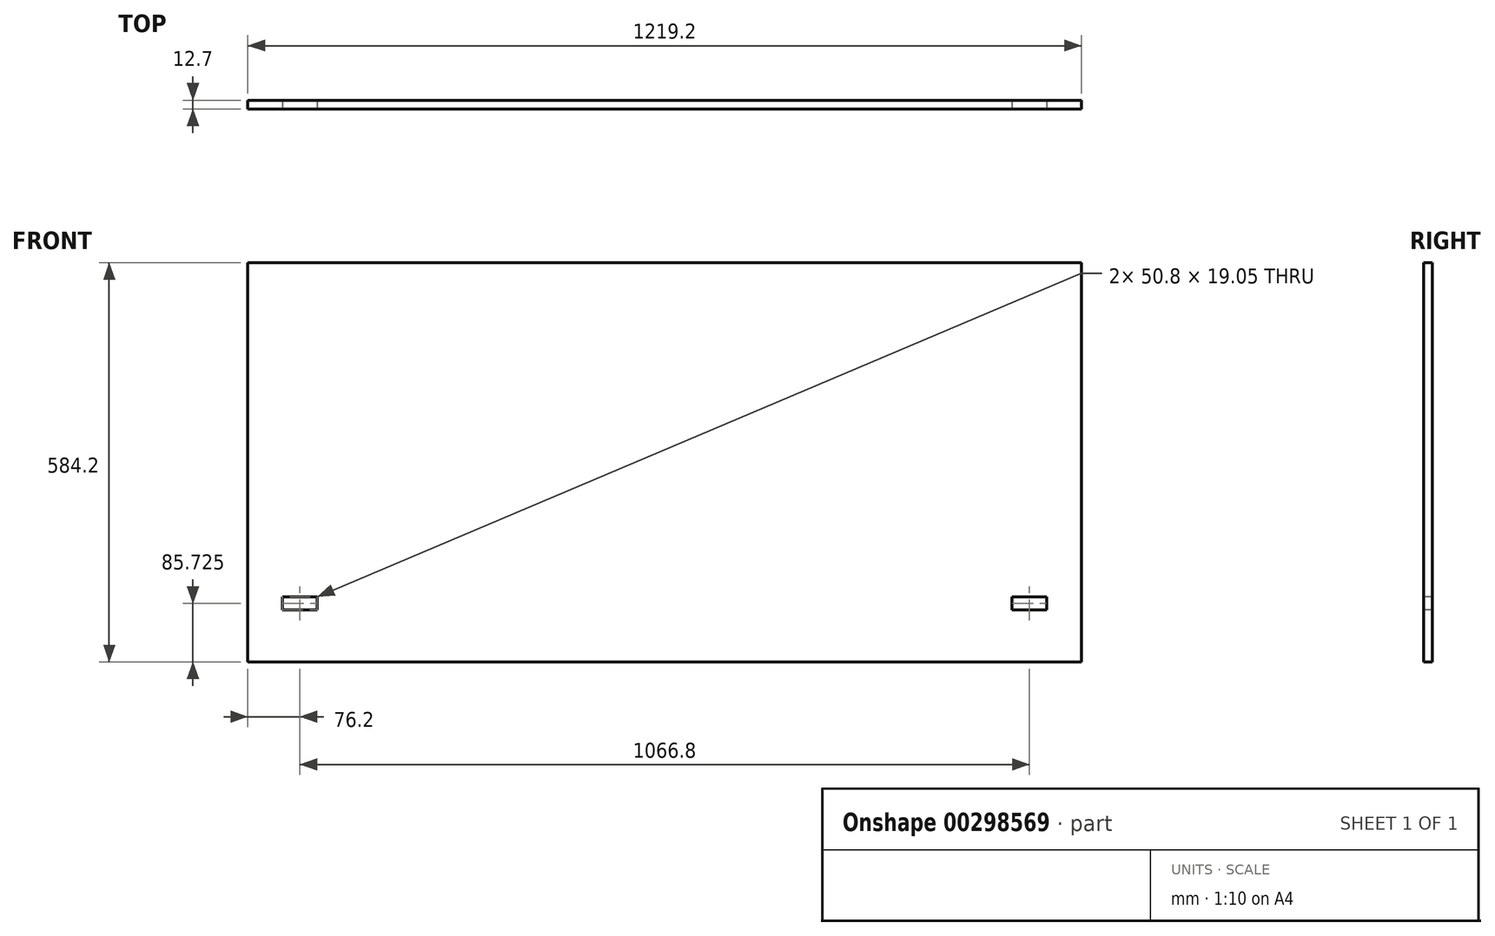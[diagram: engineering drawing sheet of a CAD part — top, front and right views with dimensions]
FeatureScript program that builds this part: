
annotation { "Feature Type Name" : "Feature", "Feature Type Description" : "" }
export const myFeature = defineFeature(function(context is Context, id is Id, definition is map)
    precondition{}
    {
        {
            assignVariable(context, id + "F0", {"name" : "thickness", "anyValue" : 12.7 * mm});
        }
        {
            var Q0;
            Q0=qCreatedBy(makeId("Front.planeOp"),FACE);
            var sketch = newSketch(context, id + "F1", { "sketchPlane" : qUnion([Q0])});
            skLineSegment(sketch, "E0", {"start": v(0, 0) * mm, "end": v(-609.6, 0) * mm});
            skLineSegment(sketch, "E1", {"start": v(-609.6, 584.2) * mm, "end": v(0, 584.2) * mm});
            skLineSegment(sketch, "E2", {"start": v(0, 584.2) * mm, "end": v(0, 0) * mm});
            skLineSegment(sketch, "E3", {"start": v(-609.6, 584.2) * mm, "end": v(-609.6, 0) * mm});
            skLineSegment(sketch, "E4.bottom", {"start": v(-558.8, 95.25) * mm, "end": v(-508, 95.25) * mm});
            skLineSegment(sketch, "E4.top", {"start": v(-558.8, 76.2) * mm, "end": v(-508, 76.2) * mm});
            skLineSegment(sketch, "E4.left", {"start": v(-558.8, 95.25) * mm, "end": v(-558.8, 76.2) * mm});
            skLineSegment(sketch, "E4.right", {"start": v(-508, 95.25) * mm, "end": v(-508, 76.2) * mm});
            skSolve(sketch);
        }
        {
            var Q0;
            Q0 = qSketchRegion(id + "F1", true);
            extrude(context, id + "F2", {"entities" : qUnion([Q0]), "oppositeDirection" : true, "depth" : getVariable(context, 'thickness')});
        }
        {
            var Q0;
            Q0=makeQuery(id+"F2.opExtrude","SWEPT_BODY",BODY,{"disambiguationData":[OSD([sQuery(id+"F1.wireOp",EDGE,"E0"),sQuery(id+"F1.wireOp",EDGE,"3tMfJS4N-ypb9-l0Ta-9uWP-DEAdmuzVW53T"),sQuery(id+"F1.wireOp",EDGE,"jTk7peYf-2WaW-bSmY-uFjm-mRNM38bE61Lu"),sQuery(id+"F1.wireOp",EDGE,"8JaLhZk6-0cRP-R6hW-y9Vx-7hvVqPKNujpa"),sQuery(id+"F1.wireOp",EDGE,"TZnCuJOO-Qegh-hEIp-s20Q-fgZjGuWCg3vA"),sQuery(id+"F1.wireOp",EDGE,"tWWneQS6-UdGj-g5Fi-xo0S-2rr6tD82CQqT"),sQuery(id+"F1.wireOp",EDGE,"b8hwCOqo-nM54-PEK6-M3np-szgyElorNUvT"),sQuery(id+"F1.wireOp",EDGE,"7F31Xd9x-INzy-KnOs-3kYU-8WDCusqLbkJ0"),sQuery(id+"F1.wireOp",EDGE,"hYDcJfnw-XkOK-fOym-D8zb-R2Y2sOVZZuOK"),sQuery(id+"F1.wireOp",EDGE,"9lJIcL2o-SPeb-7oC6-sUFb-yPgbFpKkTIm6"),sQuery(id+"F1.wireOp",EDGE,"lioOfQHn-mJ2w-PqYM-xibh-QE0FSVLkZLlc"),sQuery(id+"F1.wireOp",EDGE,"yiOthWJt-mPfk-9UEe-1KvM-reueNEaVAevJ"),sQuery(id+"F1.wireOp",EDGE,"gPYPsZx8-Czem-Lv42-KuP6-J9U4XgOXf9pq"),sQuery(id+"F1.wireOp",EDGE,"UfnbemdW-929Q-INjx-RDmx-ac4GmVFYn7Om"),sQuery(id+"F1.wireOp",EDGE,"E1"),sQuery(id+"F1.wireOp",EDGE,"E2")])]});
            var Q1;
            Q1=qCreatedBy(makeId("Right.planeOp"),FACE);
            mirror(context, id + "F3", {"operationType" : NewBodyOperationType.ADD, "entities" : qUnion([Q0]), "mirrorPlane" : qUnion([Q1])});
        }
    });
